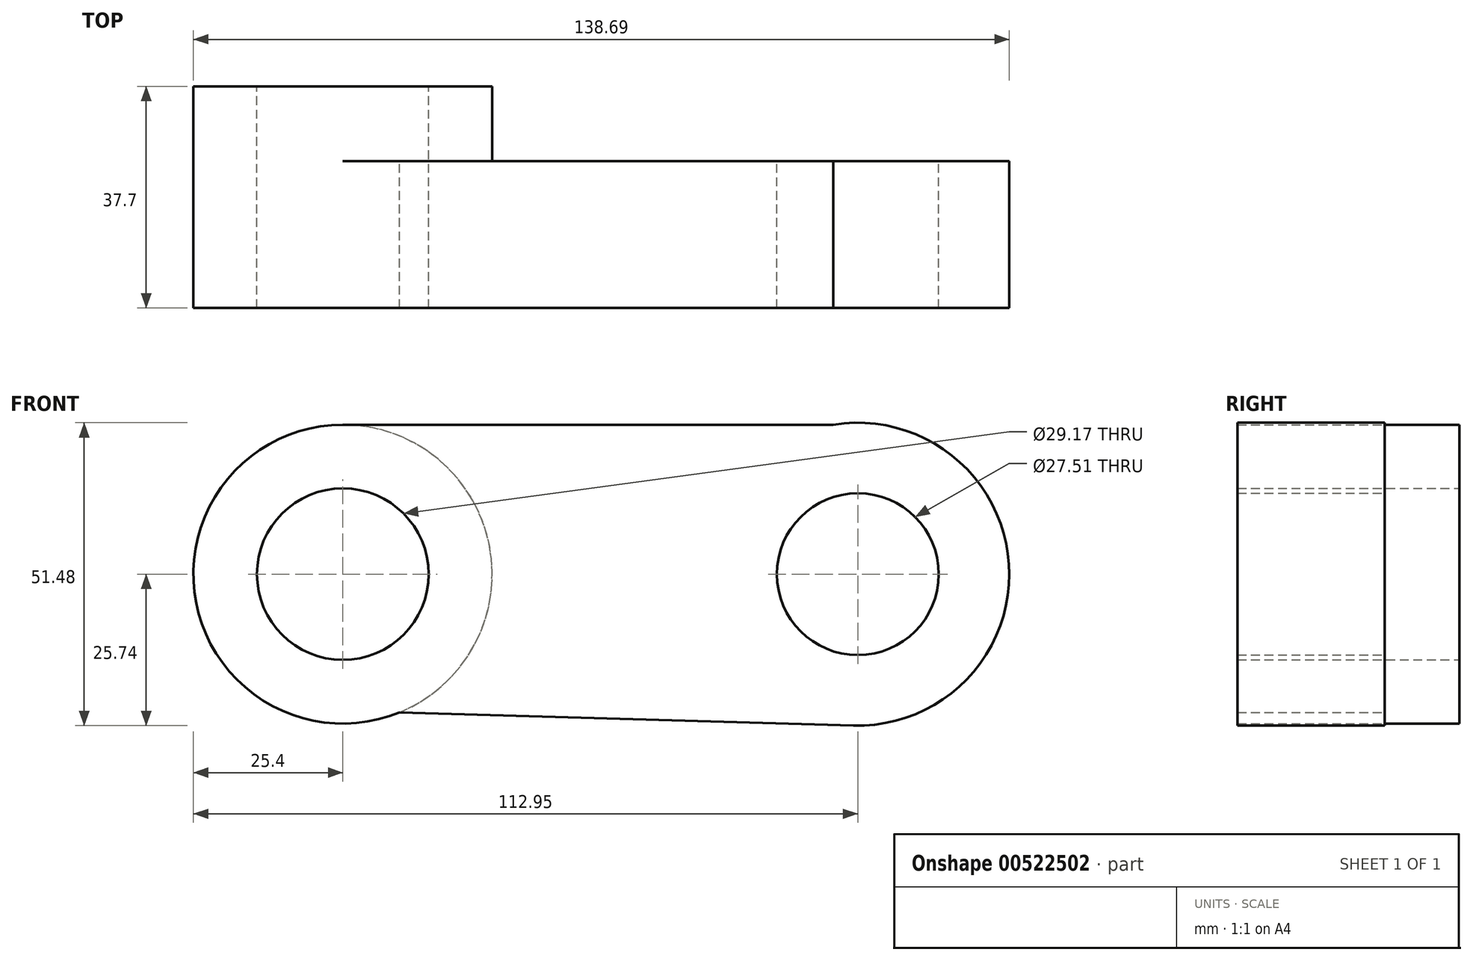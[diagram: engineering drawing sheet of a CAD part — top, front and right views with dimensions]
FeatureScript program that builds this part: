
annotation { "Feature Type Name" : "Feature", "Feature Type Description" : "" }
export const myFeature = defineFeature(function(context is Context, id is Id, definition is map)
    precondition{}
    {
        {
            var Q0;
            Q0=qCreatedBy(makeId("Front.planeOp"),FACE);
            var sketch = newSketch(context, id + "F0", { "sketchPlane" : qUnion([Q0])});
            skCircle(sketch, "E0", {"center": v(0, 0) * mm, "radius": 25.4 * mm});
            skCircle(sketch, "E1", {"center": v(87.55, 0) * mm, "radius": 25.74 * mm});
            skLineSegment(sketch, "E2", {"start": v(0, 25.4) * mm, "end": v(83.38, 25.4) * mm});
            skLineSegment(sketch, "E3", {"start": v(9.64, -23.5) * mm, "end": v(86.8, -25.73) * mm});
            skCircle(sketch, "E4", {"center": v(0, 0) * mm, "radius": 14.59 * mm});
            skCircle(sketch, "E5", {"center": v(87.55, 0) * mm, "radius": 13.76 * mm});
            skSolve(sketch);
        }
        {
            var Q0;
            Q0=makeQuery(id+"F0.imprint","IMPRINT",FACE,{"disambiguationData":[TD([[makeQuery(id+"F0.imprint","IMPRINT",EDGE,{"derivedFrom":sQuery(id+"F0.wireOp",EDGE,"E4")}),-1.0]])]});
            var Q1;
            {var subQ0=sQuery(id+"F0.wireOp",EDGE,"E2");Q1=makeQuery(id+"F0.imprint","IMPRINT",FACE,{"disambiguationData":[TD([[makeQuery(id+"F0.imprint","IMPRINT",EDGE,{"derivedFrom":subQ0}),-1.0]])]});}
            var Q2;
            Q2=makeQuery(id+"F0.imprint","IMPRINT",FACE,{"disambiguationData":[TD([[makeQuery(id+"F0.imprint","IMPRINT",EDGE,{"derivedFrom":sQuery(id+"F0.wireOp",EDGE,"E5")}),-1.0]])]});
            extrude(context, id + "F1", {"entities" : qUnion([Q0, Q1, Q2]), "depth" : 25 * mm, "offsetDistance" : 25.4 * mm});
        }
        {
            var Q0;
            Q0=makeQuery(id+"F0.imprint","IMPRINT",FACE,{"disambiguationData":[TD([[makeQuery(id+"F0.imprint","IMPRINT",EDGE,{"derivedFrom":sQuery(id+"F0.wireOp",EDGE,"E4")}),-1.0]])]});
            extrude(context, id + "F2", {"entities" : qUnion([Q0]), "operationType" : NewBodyOperationType.ADD, "oppositeDirection" : true, "depth" : 12.7 * mm, "offsetDistance" : 25.4 * mm});
        }
    });
